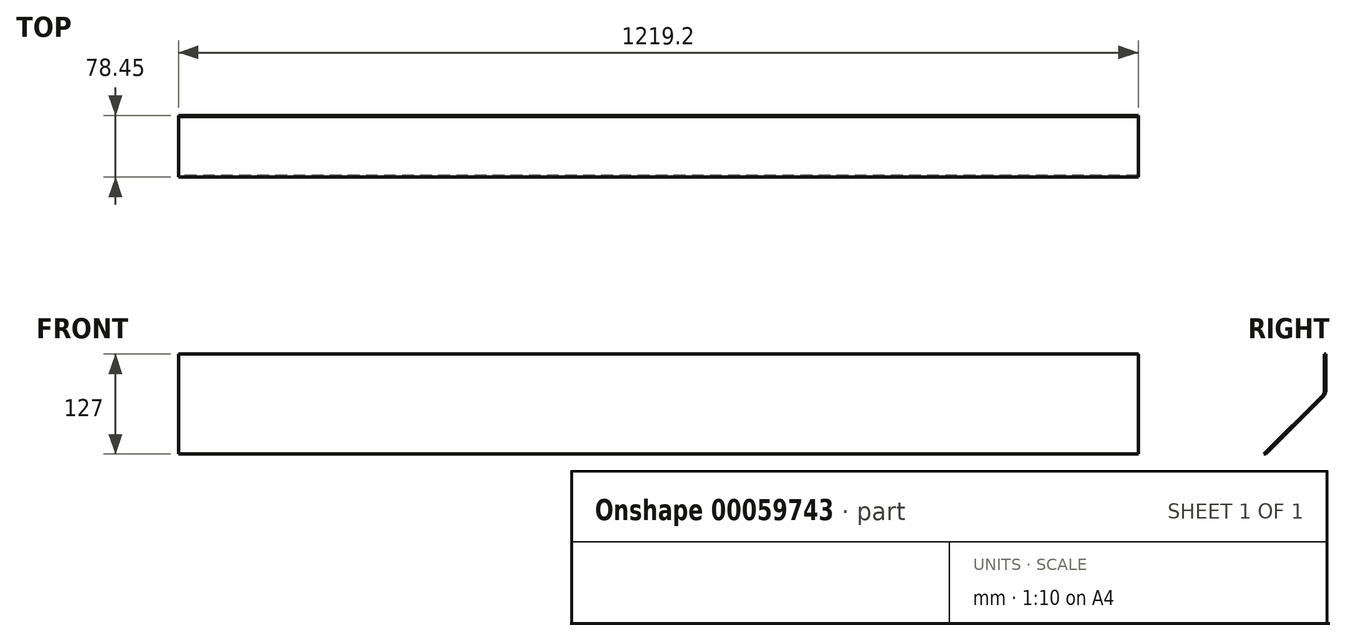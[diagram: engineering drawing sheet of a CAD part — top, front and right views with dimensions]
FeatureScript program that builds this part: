
annotation { "Feature Type Name" : "Feature", "Feature Type Description" : "" }
export const myFeature = defineFeature(function(context is Context, id is Id, definition is map)
    precondition{}
    {
        {
            var Q0;
            Q0=qCreatedBy(makeId("Right.planeOp"),FACE);
            var sketch = newSketch(context, id + "F0", { "sketchPlane" : qUnion([Q0])});
            skLineSegment(sketch, "E0", {"start": v(0, 50.8) * mm, "end": v(0, 5.26) * mm});
            skLineSegment(sketch, "E1", {"start": v(-3.72, -3.72) * mm, "end": v(-76.2, -76.2) * mm});
            skLineSegment(sketch, "E2.0", {"start": v(-5.3, -3.06) * mm, "end": v(-78.45, -76.2) * mm});
            skLineSegment(sketch, "E2.1", {"start": v(-1.59, 50.8) * mm, "end": v(-1.59, 5.92) * mm});
            skPoint(sketch, "E3.visualSharp", {"position": v(-1.59, 0.66) * mm});
            skArc(sketch, "E3.filletArc", {"start": v(-5.3, -3.06) * mm, "mid": v(-2.55, 1.06) * mm, "end": v(-1.59, 5.92) * mm});
            skPoint(sketch, "E4.visualSharp", {"position": v(0, 0) * mm});
            skArc(sketch, "E4.filletArc", {"start": v(-3.72, -3.72) * mm, "mid": v(-0.97, 0.4) * mm, "end": v(0, 5.26) * mm});
            skLineSegment(sketch, "E5", {"start": v(-78.45, -76.2) * mm, "end": v(-76.2, -76.2) * mm});
            skLineSegment(sketch, "E6", {"start": v(-1.59, 50.8) * mm, "end": v(0, 50.8) * mm});
            skSolve(sketch);
        }
        {
            var Q0;
            Q0=qSketchRegion(id+"F0",true);
            extrude(context, id + "F1", {"entities" : qUnion([Q0]), "depth" : 609.6 * mm, "hasSecondDirection" : true, "secondDirectionOppositeDirection" : true, "secondDirectionDepth" : 609.6 * mm});
        }
    });
